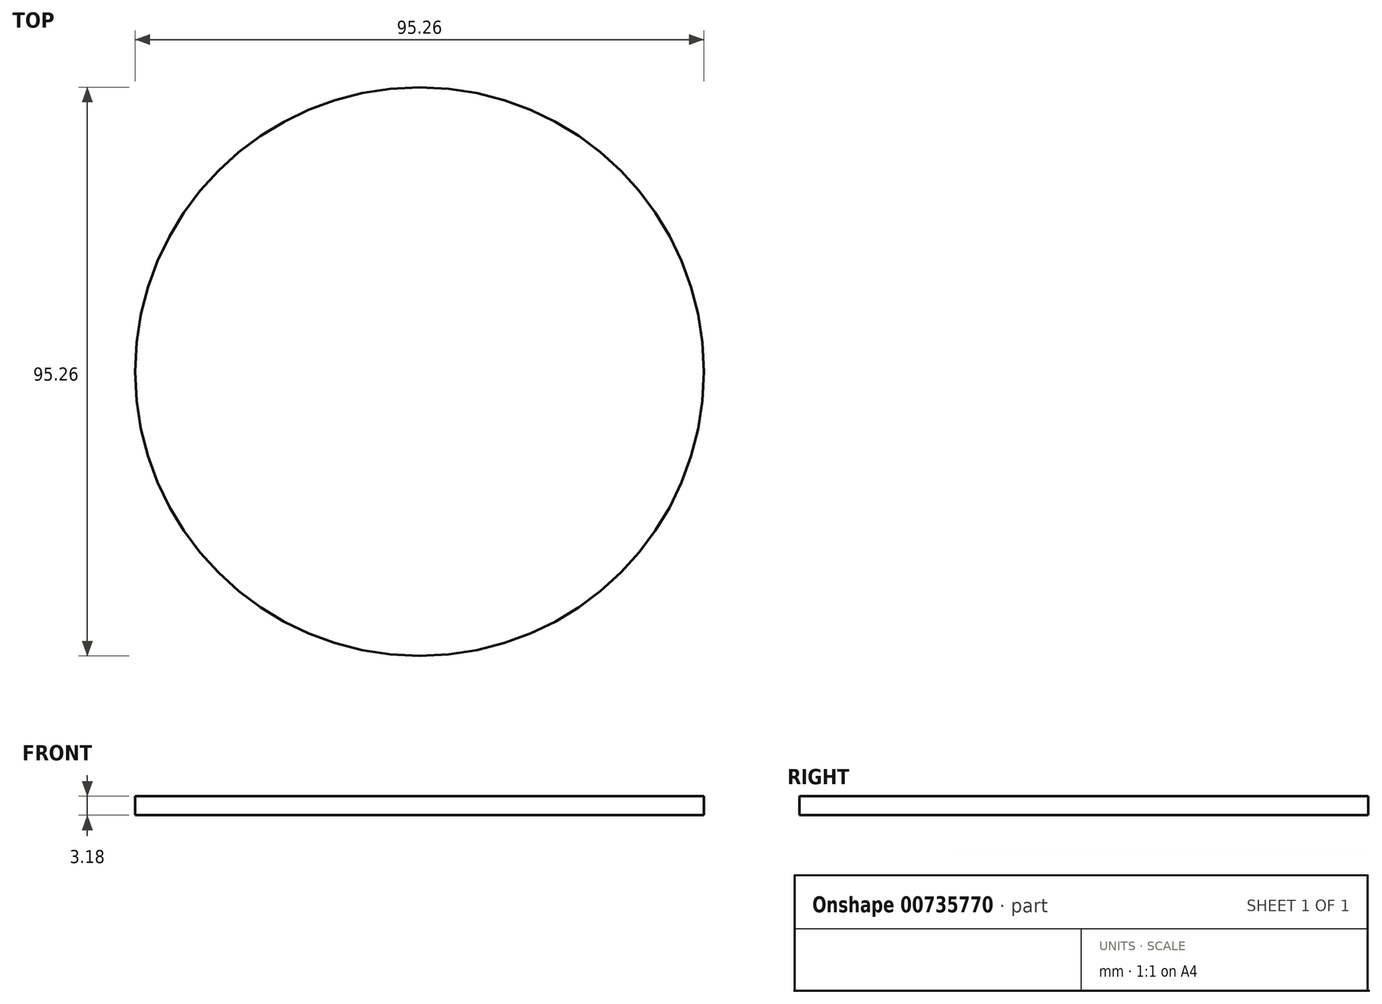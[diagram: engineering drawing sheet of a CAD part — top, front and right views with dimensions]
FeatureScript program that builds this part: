
annotation { "Feature Type Name" : "Feature", "Feature Type Description" : "" }
export const myFeature = defineFeature(function(context is Context, id is Id, definition is map)
    precondition{}
    {
        {
            var Q0;
            Q0=qCreatedBy(makeId("Top.planeOp"),FACE);
            var sketch = newSketch(context, id + "F0", { "sketchPlane" : qUnion([Q0])});
            skCircle(sketch, "E0", {"center": v(0, 0) * mm, "radius": 47.63 * mm});
            skSolve(sketch);
        }
        {
            var Q0;
            Q0=makeQuery(id+"F0.imprint","IMPRINT",FACE,{"disambiguationData":[TD([[makeQuery(id+"F0.imprint","IMPRINT",EDGE,{"derivedFrom":sQuery(id+"F0.wireOp",EDGE,"E0")}),1.0]])]});
            extrude(context, id + "F1", {"entities" : qUnion([Q0]), "depth" : 3.17 * mm, "offsetDistance" : 25.4 * mm});
        }
    });
